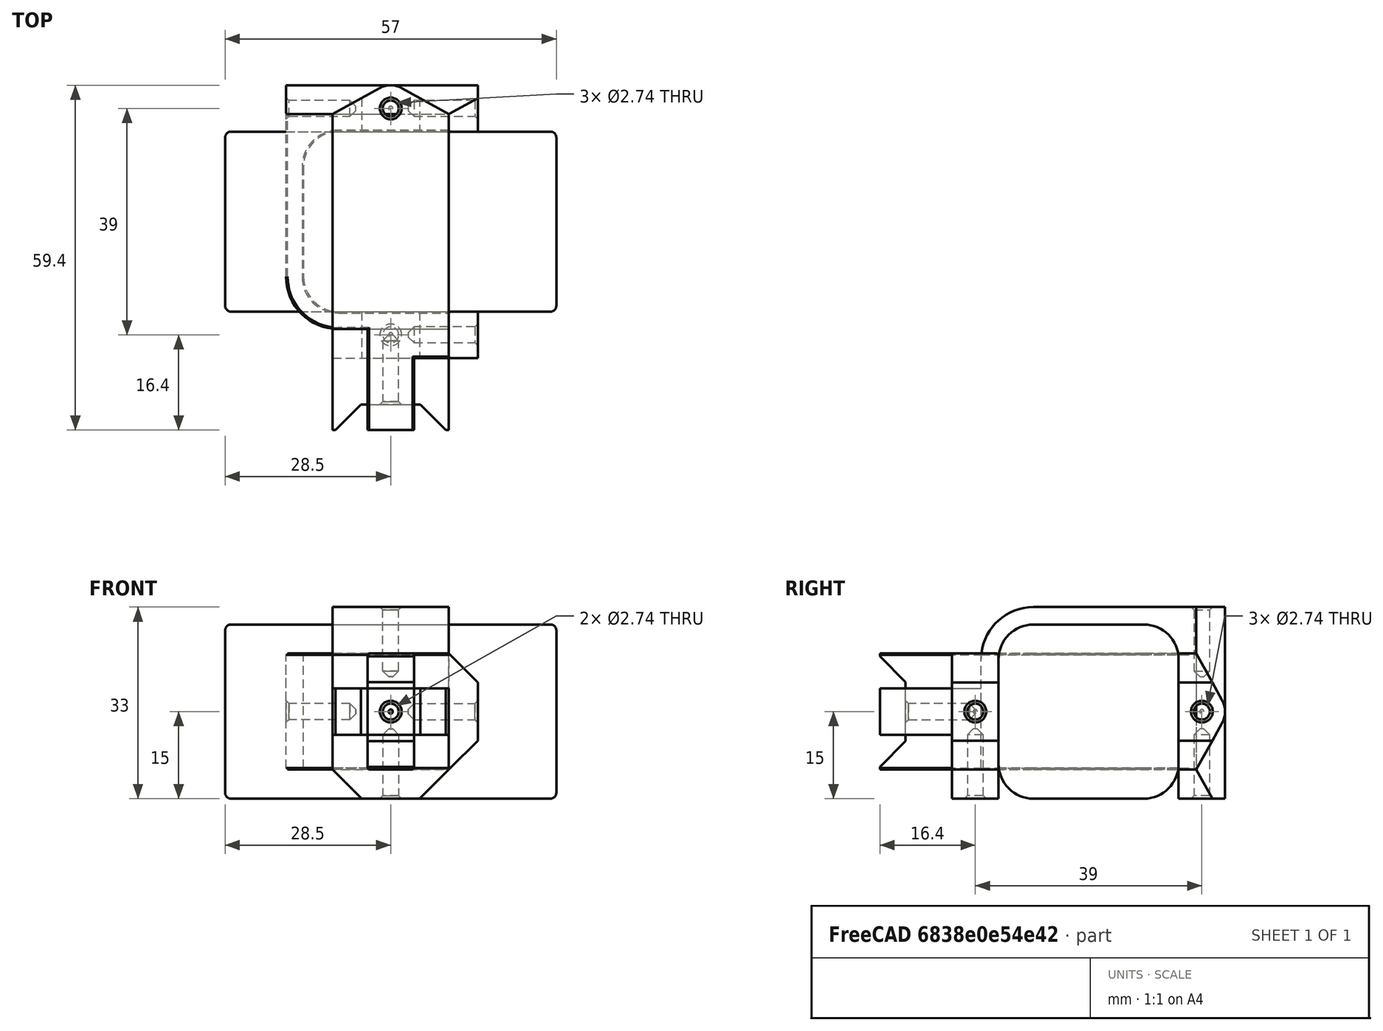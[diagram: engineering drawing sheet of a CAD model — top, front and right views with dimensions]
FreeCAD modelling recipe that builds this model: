
FCSTD DOCUMENT  (FreeCAD 0.17R10654 (Git))
Label: battery-bracket-ng
License: The MIT License
LicenseURL: http://opensource.org/licenses/MIT
objects: Sketcher::SketchObject×6, PartDesign::Pad×3, PartDesign::Pocket×3, PartDesign::Chamfer×3, PartDesign::Fillet×2, Part::Feature×1, App::DocumentObjectGroup×1, PartDesign::Mirrored×1, PartDesign::Body×1, App::Part×1, Mesh::Feature×1, Part::FeaturePython×1, Part::Chamfer×1
note: 28 computed .brp shape members not serialized (recipe doc carries the construction recipe); baked Part::Feature solids carry a one-line shape summary decoded from their .brp

FEATURE [Sketcher::SketchObject] Sketch  label="bracket-sketch"
  MapMode = 5
  Placement = pos=(0,0,0) rot=(0.57735,0.57735,0.57735;2.0944rad)
  Support = -> [YZ_Plane001]
  sketch-geometry (12):
    g0: LineSegment StartX=4 StartY=4 StartZ=0 EndX=17 EndY=4 EndZ=0
    g1: LineSegment StartX=17 StartY=4 StartZ=0 EndX=17 EndY=18 EndZ=0
    g2: LineSegment StartX=17 StartY=18 StartZ=0 EndX=54 EndY=18 EndZ=0
    g3: LineSegment StartX=54 StartY=18 StartZ=0 EndX=54 EndY=-15 EndZ=0
    g4: LineSegment StartX=54 StartY=-15 StartZ=0 EndX=51 EndY=-15 EndZ=0
    g5: LineSegment StartX=51 StartY=-15 StartZ=0 EndX=51 EndY=15 EndZ=0
    g6: LineSegment StartX=51 StartY=15 StartZ=0 EndX=20 EndY=15 EndZ=0
    g7: LineSegment StartX=20 StartY=15 StartZ=0 EndX=20 EndY=-15 EndZ=0
    g8: LineSegment StartX=20 StartY=-15 StartZ=0 EndX=12 EndY=-15 EndZ=0
    g9: LineSegment StartX=12 StartY=-15 StartZ=0 EndX=12 EndY=-4 EndZ=0
    g10: LineSegment StartX=12 StartY=-4 StartZ=0 EndX=4 EndY=-4 EndZ=0
    g11: LineSegment StartX=4 StartY=-4 StartZ=0 EndX=4 EndY=4 EndZ=0
  constraints (36):
    c: Horizontal(g0)
    c: Coincident(g0,g1)
    c: Vertical(g1)
    c: Coincident(g1,g2)
    c: Horizontal(g2)
    c: Coincident(g2,g3)
    c: Vertical(g3)
    c: Coincident(g3,g4)
    c: Horizontal(g4)
    c: Coincident(g4,g5)
    c: Vertical(g5)
    c: Coincident(g5,g6)
    c: Horizontal(g6)
    c: Coincident(g6,g7)
    c: Coincident(g7,g8)
    c: Horizontal(g8)
    c: Coincident(g8,g9)
    c: Vertical(g9)
    c: Coincident(g9,g10)
    c: Horizontal(g10)
    c: Coincident(g10,g11)
    c: Vertical(g11)
    c: Vertical(g7)
    c: Coincident(g0,g11)
    c: Symmetric(g0,g10,g-1)
    c: DistanceY(g11) = 8
    c: DistanceX(g-1,g10) = 4
    c: DistanceY(g-1,g1) = 18
    c: DistanceY(g-1,g8) = -15
    c: DistanceY(g-1,g3) = -15
    c: DistanceX(g6) = -31
    c: DistanceY(g7) = -30
    c: DistanceX(g4) = -3
    c: DistanceX(g0,g6) = 3
    c: DistanceX(g8) = -8
    c: DistanceX(g10) = -8
FEATURE [PartDesign::Pad] Pad  label="bracket-pad"
  Length = 20
  Length2 = 100
  Midplane = true
  Placement = pos=(0,0,0) rot=(0.57735,0.57735,0.57735;2.0944rad)
  Profile = -> Sketch
  Type = 0
FEATURE [Sketcher::SketchObject] Sketch001  label="motor-bracket-screw-hole-sketch"
  MapMode = 5
  Placement = pos=(0,4,0) rot=(-0.57735,-0.57735,0.57735;4.18879rad)
  Support = -> [Pad]
  sketch-geometry (1):
    g0: Circle CenterX=0 CenterY=0 CenterZ=0 NormalX=0 NormalY=0 NormalZ=1 Radius=1.37
  constraints (2):
    c: Coincident(g0,g-1)
    c: Radius(g0) = 1.37
FEATURE [PartDesign::Pocket] Pocket  label="motor-bracket-screw-hole-pocket"
  BaseFeature = -> Pad
  Length = 12
  Placement = pos=(0,0,0) rot=(0.57735,0.57735,0.57735;2.0944rad)
  Profile = -> Sketch001
  Type = 0
FEATURE [Sketcher::SketchObject] Sketch002  label="bracket-rear-sketch"
  MapMode = 5
  Placement = pos=(0,0,18) rot=(0,0,-1;1.5708rad)
  Support = -> [Pocket]
  sketch-geometry (4):
    g0: ArcOfCircle CenterX=-55 CenterY=0 CenterZ=0 NormalX=0 NormalY=0 NormalZ=1 Radius=4 StartAngle=2.63257 EndAngle=3.65061
    g1: LineSegment StartX=-58.4929 StartY=1.94929 StartZ=0 EndX=-54 EndY=10 EndZ=0
    g2: LineSegment StartX=-54 StartY=10 StartZ=0 EndX=-54 EndY=-10 EndZ=0
    g3: LineSegment StartX=-54 StartY=-10 StartZ=0 EndX=-58.4929 EndY=-1.94929 EndZ=0
  constraints (13):
    c: PointOnObject(g0,g-1)
    c: DistanceX(g-1,g0) = -55
    c: Radius(g0) = 4
    c: Coincident(g1,g2)
    c: Coincident(g2,g3)
    c: Coincident(g1,g0)
    c: Coincident(g3,g0)
    c: Tangent(g0,g1)
    c: Tangent(g0,g3)
    c: Equal(g3,g1)
    c: DistanceY(g2) = -20
    c: Vertical(g2)
    c: DistanceX(g2,g0) = -1
FEATURE [PartDesign::Pad] Pad001  label="bracket-rear-pad"
  BaseFeature = -> Pocket
  Length = 33
  Length2 = 100
  Placement = pos=(0,0,0) rot=(0.57735,0.57735,0.57735;2.0944rad)
  Profile = -> Sketch002
  Reversed = true
  Type = 0
FEATURE [Sketcher::SketchObject] Sketch003  label="top-screw-hole-sketch"
  MapMode = 5
  Placement = pos=(0,0,18) rot=(0,0,-1;1.5708rad)
  Support = -> [Pad001]
  sketch-geometry (1):
    g0: Circle CenterX=-55 CenterY=0 CenterZ=0 NormalX=0 NormalY=0 NormalZ=1 Radius=1.37
  constraints (3):
    c: PointOnObject(g0,g-1)
    c: DistanceX(g-1,g0) = -55
    c: Radius(g0) = 1.37
FEATURE [PartDesign::Pocket] Pocket001  label="top-screw-hole-pocket"
  BaseFeature = -> Pad001
  Length = 12
  Placement = pos=(0,0,0) rot=(0.57735,0.57735,0.57735;2.0944rad)
  Profile = -> Sketch003
  Type = 0
FEATURE [Sketcher::SketchObject] Sketch004  label="bottom-screw-holes-sketch"
  MapMode = 5
  Placement = pos=(0,0,-15) rot=(0.707107,0.707107,0;3.14159rad)
  Support = -> [Pocket001]
  sketch-geometry (2):
    g0: Circle CenterX=55 CenterY=0 CenterZ=0 NormalX=0 NormalY=0 NormalZ=1 Radius=1.37
    g1: Circle CenterX=16 CenterY=0 CenterZ=0 NormalX=0 NormalY=0 NormalZ=1 Radius=1.37
  constraints (6):
    c: PointOnObject(g0,g-1)
    c: PointOnObject(g1,g-1)
    c: Radius(g1) = 1.37
    c: Radius(g0) = 1.37
    c: DistanceX(g-1,g0) = 55
    c: DistanceX(g-1,g1) = 16
FEATURE [PartDesign::Pocket] Pocket002  label="bottom-screw-holes-pocket"
  BaseFeature = -> Pocket001
  Length = 12
  Placement = pos=(0,0,0) rot=(0.57735,0.57735,0.57735;2.0944rad)
  Profile = -> Sketch004
  Type = 0
FEATURE [Part::Feature] Part__Feature  label="battery"
  Placement = pos=(0,35.5,0) rot=(0,0,1;0rad)
  shape: bbox 57 x 31.99 x 30.99 mm, 26 faces (baked)
FEATURE [App::DocumentObjectGroup] Group  label="components"
  Group = -> [Part__Feature]
FEATURE [PartDesign::Fillet] Fillet
  Base = -> Pocket002 [Edge47,Edge46]
  BaseFeature = -> Pocket002
  Placement = pos=(0,0,0) rot=(0.57735,0.57735,0.57735;2.0944rad)
  Radius = 6
FEATURE [PartDesign::Fillet] Fillet001
  Base = -> Fillet [Edge45]
  BaseFeature = -> Fillet
  Placement = pos=(0,0,0) rot=(0.57735,0.57735,0.57735;2.0944rad)
  Radius = 9
FEATURE [PartDesign::Chamfer] Chamfer
  Base = -> Fillet001 [Edge8,Edge37,Edge11,Edge45]
  BaseFeature = -> Fillet001
  Placement = pos=(0,0,0) rot=(0.57735,0.57735,0.57735;2.0944rad)
  Size = 5
FEATURE [Sketcher::SketchObject] Sketch005
  ExternalGeometry = -> [Chamfer]
  MapMode = 5
  Placement = pos=(0,0,4) rot=(0,0,-1;1.5708rad)
  Support = -> [Chamfer]
  sketch-geometry (4):
    g0: LineSegment StartX=-4.1 StartY=10 StartZ=0 EndX=-4.1 EndY=5 EndZ=0
    g1: LineSegment StartX=-4.1 StartY=5 StartZ=0 EndX=0.4 EndY=9.5 EndZ=0
    g2: LineSegment StartX=0.4 StartY=9.5 StartZ=0 EndX=0.4 EndY=10 EndZ=0
    g3: LineSegment StartX=0.4 StartY=10 StartZ=0 EndX=-4.1 EndY=10 EndZ=0
  constraints (12):
    c: Coincident(g0,g1)
    c: Coincident(g1,g2)
    c: Vertical(g2)
    c: Coincident(g2,g3)
    c: Coincident(g3,g0)
    c: Horizontal(g3)
    c: Vertical(g0)
    c: Angle(g1,g0) = 0.785398
    c: DistanceY(g2,g2) = 0.5
    c: PointOnObject(g-3,g3)
    c: DistanceX(g0,g-3) = 0.1
    c: DistanceY(g0) = 5
FEATURE [PartDesign::Pad] Pad002
  BaseFeature = -> Chamfer
  Length = 8
  Length2 = 100
  Placement = pos=(0,0,0) rot=(0.57735,0.57735,0.57735;2.0944rad)
  Profile = -> Sketch005
  Reversed = true
  Type = 0
FEATURE [PartDesign::Mirrored] Mirrored
  BaseFeature = -> Pad002
  MirrorPlane = -> YZ_Plane001
  Originals = -> [Pad002]
  Placement = pos=(0,0,0) rot=(0.57735,0.57735,0.57735;2.0944rad)
FEATURE [PartDesign::Chamfer] Chamfer001
  Base = -> Mirrored [Edge61,Edge63,Edge85,Edge80]
  BaseFeature = -> Mirrored
  Placement = pos=(0,0,0) rot=(0.57735,0.57735,0.57735;2.0944rad)
  Size = 1
FEATURE [PartDesign::Chamfer] Chamfer002
  Base = -> Chamfer001 [Edge3,Edge83,Edge80,Edge77]
  BaseFeature = -> Chamfer001
  Placement = pos=(0,0,0) rot=(0.57735,0.57735,0.57735;2.0944rad)
  Size = 0.5
FEATURE [PartDesign::Body] Pocket002Body
  Group = -> [Sketch,Pad,Sketch001,Pocket,Sketch002,Pad001,Sketch003,Pocket001,Sketch004,Pocket002,Fillet,Fillet001,Chamfer,Sketch005,Pad002,Mirrored,Chamfer001,Chamfer002]
  Origin = -> Pocket002BodyOrigin
  Tip = -> Chamfer002
FEATURE [App::Part] Part
  Group = -> [Pocket002Body]
  License = CC BY 3.0
  LicenseURL = http://creativecommons.org/licenses/by/3.0/
  Origin = -> PartOrigin
FEATURE [Mesh::Feature] _2_battery_bracket  label="02-battery-bracket"
FEATURE [Part::FeaturePython] Clone  label="Chamfer004"  # Draft clone (typed FeaturePython)
  AttacherType = Attacher::AttachEngine3D
  Objects = -> [Chamfer002]
  Placement = pos=(0,0,0) rot=(0,0,1;1.5708rad)
  Scale = (1,1,1)
FEATURE [Part::Chamfer] Chamfer003  label="Chamfer005"
  Base = -> Clone
  Edges = 22 edges r=0.25: [Edge8,Edge11,Edge16,Edge17,Edge18,Edge19,Edge20,Edge22,Edge23,Edge25,Edge26,Edge27,Edge29,Edge34,Edge35,Edge37,Edge38,Edge40,Edge41,Edge42,Edge43,Edge44]
